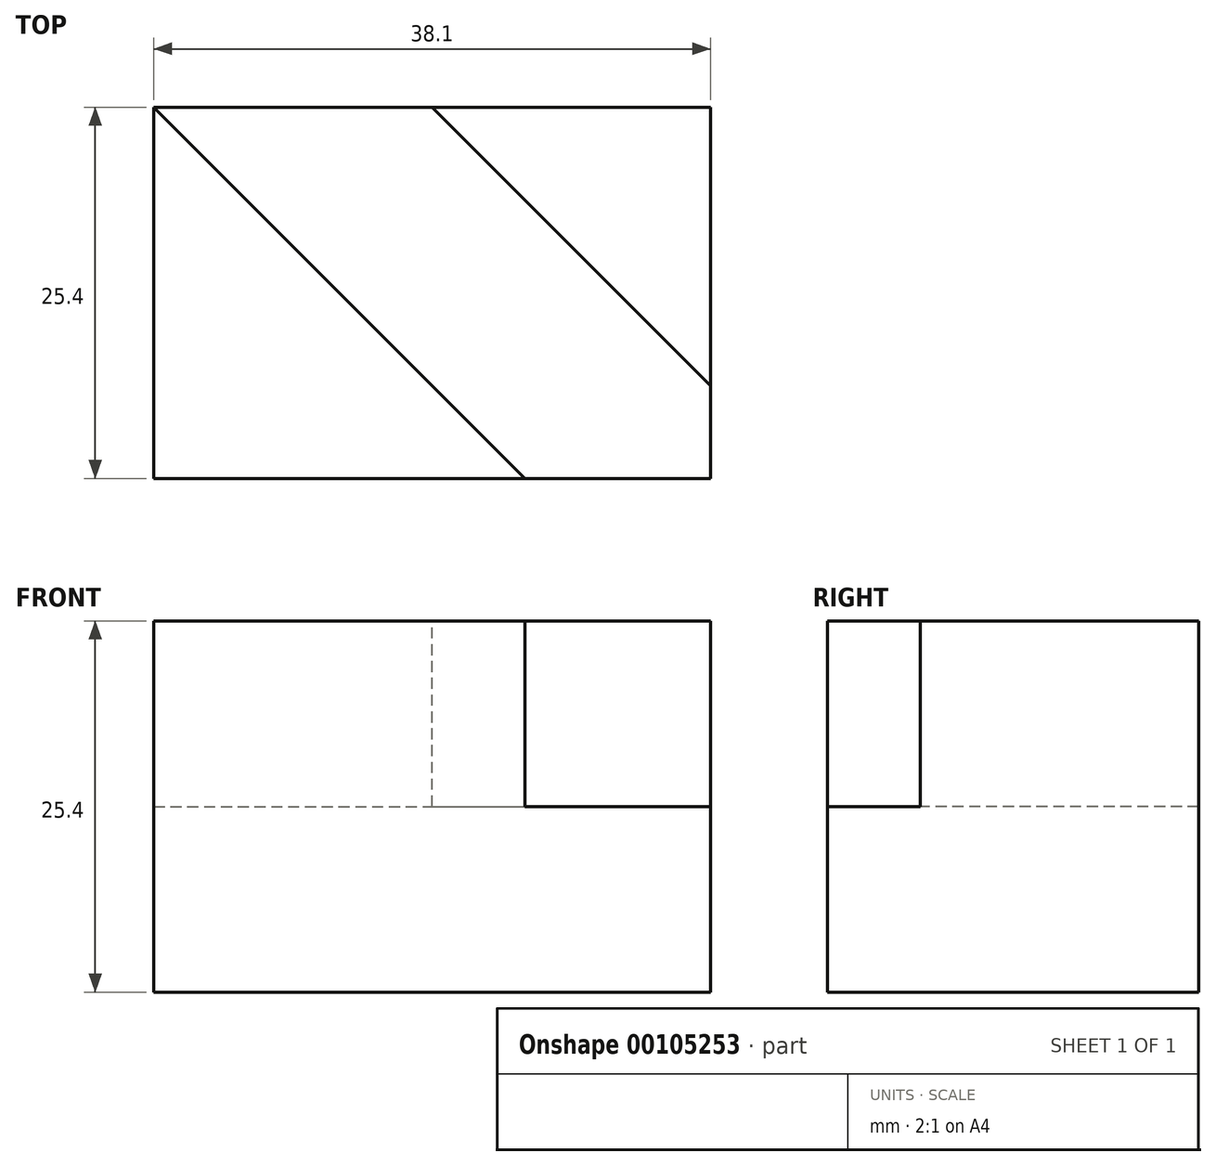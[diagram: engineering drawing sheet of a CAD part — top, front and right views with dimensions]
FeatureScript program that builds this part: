
annotation { "Feature Type Name" : "Feature", "Feature Type Description" : "" }
export const myFeature = defineFeature(function(context is Context, id is Id, definition is map)
    precondition{}
    {
        {
            var Q0;
            Q0=qCreatedBy(makeId("Front.planeOp"),FACE);
            var sketch = newSketch(context, id + "F0", { "sketchPlane" : qUnion([Q0])});
            skLineSegment(sketch, "E0.bottom", {"start": v(0, 0) * mm, "end": v(38.1, 0) * mm});
            skLineSegment(sketch, "E0.top", {"start": v(0, 25.4) * mm, "end": v(38.1, 25.4) * mm});
            skLineSegment(sketch, "E0.left", {"start": v(0, 0) * mm, "end": v(0, 25.4) * mm});
            skLineSegment(sketch, "E0.right", {"start": v(38.1, 0) * mm, "end": v(38.1, 25.4) * mm});
            skSolve(sketch);
        }
        {
            var Q0;
            Q0 = qSketchRegion(id + "F0", true);
            extrude(context, id + "F1", {"entities" : qUnion([Q0]), "depth" : 25.4 * mm});
        }
        {
            var Q0;
            Q0=makeQuery(id+"F1.opExtrude","SWEPT_FACE",FACE,{"disambiguationData":[OSD([sQuery(id+"F0.wireOp",EDGE,"E0.top")])]});
            var sketch = newSketch(context, id + "F2", { "sketchPlane" : qUnion([Q0])});
            skLineSegment(sketch, "E1", {"start": v(19.05, 0) * mm, "end": v(38.1, -19.05) * mm});
            skSolve(sketch);
        }
        {
            var Q0;
            {var subQ3=sQuery(id+"F2.wireOp",EDGE,"E1");Q0=makeQuery(id+"F2.imprint","IMPRINT",FACE,{"disambiguationData":[TD([[makeQuery(id+"F2.imprint","IMPRINT",EDGE,{"derivedFrom":subQ3}),-1.0]])]});}
            var sketch = newSketch(context, id + "F3", { "sketchPlane" : qUnion([Q0])});
            skLineSegment(sketch, "E2", {"start": v(0, 0) * mm, "end": v(25.4, -25.4) * mm});
            skSolve(sketch);
        }
        {
            var Q0;
            {var subQ6=sQuery(id+"F3.wireOp",EDGE,"E2");Q0=makeQuery(id+"F3.imprint","IMPRINT",FACE,{"disambiguationData":[TD([[makeQuery(id+"F3.imprint","IMPRINT",EDGE,{"derivedFrom":subQ6}),1.0]])]});}
            extrude(context, id + "F4", {"entities" : qUnion([Q0]), "operationType" : NewBodyOperationType.REMOVE, "oppositeDirection" : true, "depth" : 12.7 * mm});
        }
    });
